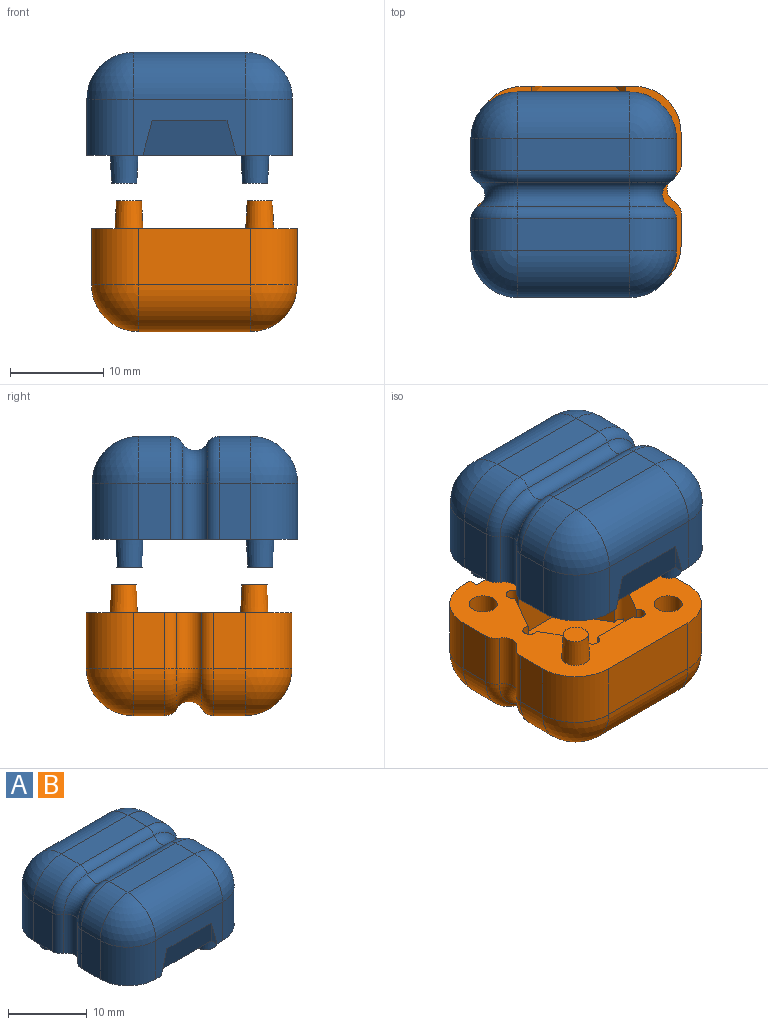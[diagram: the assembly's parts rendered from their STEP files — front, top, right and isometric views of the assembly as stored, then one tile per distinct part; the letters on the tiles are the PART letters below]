
ASSEMBLY  parts=2 mates=1
PART A: 62 faces, bbox 22.8x22x14.4 mm
  f0: plane 12x6mm, normal (0,-1,0), area 38.4mm2, adj f4,f13,f19,f22,f49,f50,f51
  f1: plane 6x3.4mm, normal (1,0,0), area 20.4mm2, adj f4,f16,f20,f52
  f2: plane 6x3.4mm, normal (-1,0,0), area 20.4mm2, adj f4,f5,f13,f61
  f3: plane 12x3.4mm, normal (0,0,1), area 40.8mm2, adj f14,f15,f20,f54
  f4: plane 22x22mm, normal (0,0,-1), area 284.7mm2, adj f0,f1,f2,f7,f8,f9,f11,f13
  f5: cylinder r=5mm len=5mm, axis (0,1,0), area 26.7mm2, adj f2,f10,f17,f60
  f6: cylinder r=5mm len=5mm, axis (0,-1,0), area 26.7mm2, adj f7,f10,f21,f58
  f7: plane 6x3.4mm, normal (1,0,0), area 20.4mm2, adj f4,f6,f22,f57
  f8: plane 12x6mm, normal (0,1,0), area 72mm2, adj f4,f11,f15,f16
  f9: plane 6x3.4mm, normal (-1,0,0), area 20.4mm2, adj f4,f11,f14,f56
  f10: plane 12x3.4mm, normal (0,0,1), area 40.8mm2, adj f5,f6,f19,f59
  f11: cylinder r=5mm len=6mm, axis (0,0,-1), area 47.1mm2, adj f4,f8,f9,f12
  f12: sphere r=5mm, area 39.3mm2, adj f11,f14,f15
  f13: cylinder r=5mm len=6mm, axis (0,0,1), area 47.1mm2, adj f0,f2,f4,f17
  f14: cylinder r=5mm len=5mm, axis (0,1,0), area 26.7mm2, adj f3,f9,f12,f55
  f15: cylinder r=5mm len=12mm, axis (1,0,0), area 94.2mm2, adj f3,f8,f12,f18
  f16: cylinder r=5mm len=6mm, axis (0,0,1), area 47.1mm2, adj f1,f4,f8,f18
  f17: sphere r=5mm, area 39.3mm2, adj f5,f13,f19
  f18: sphere r=5mm, area 39.3mm2, adj f15,f16,f20
  f19: cylinder r=5mm len=12mm, axis (-1,0,0), area 94.2mm2, adj f0,f10,f17,f21
  f20: cylinder r=5mm len=5mm, axis (0,-1,0), area 26.7mm2, adj f1,f3,f18,f53
  f21: sphere r=5mm, area 39.3mm2, adj f6,f19,f22
  f22: cylinder r=5mm len=6mm, axis (0,0,-1), area 47.1mm2, adj f0,f4,f7,f21
  f23: cylinder r=1.5mm len=6mm, axis (0,0,-1), area 18.8mm2, adj f4,f27,f56,f61
  f24: cylinder r=1.5mm len=6mm, axis (0,0,1), area 18.8mm2, adj f4,f25,f52,f57
  f25: torus R=5mm, axis (0,-1,0), area 18.6mm2, adj f24,f26,f53,f58
  f26: cylinder r=1.5mm len=12mm, axis (-1,0,0), area 37.7mm2, adj f25,f27,f54,f59
  f27: torus R=5mm, axis (0,-1,0), area 18.6mm2, adj f23,f26,f55,f60
  f28: cylinder r=0.75mm len=6mm, axis (0,0,-1), area 18.8mm2, adj f4,f29,f39,f40
  f29: plane 6x5.43mm, normal (0,1,0), area 32.6mm2, adj f4,f28,f30,f40
  f30: cylinder r=0.75mm len=6mm, axis (0,0,-1), area 18.8mm2, adj f4,f29,f31,f40
  f31: plane 6x4.7mm, normal (0.87,0.5,0), area 32.6mm2, adj f4,f30,f32,f40
  f32: cylinder r=0.75mm len=6mm, axis (0,0,-1), area 18.8mm2, adj f4,f31,f33,f40
  f33: plane 6x4.7mm, normal (0.87,-0.5,0), area 32.6mm2, adj f4,f32,f34,f40
  f34: cylinder r=0.75mm len=6mm, axis (0,0,-1), area 18.8mm2, adj f4,f33,f35,f40
  f35: plane 6x5.43mm, normal (0,-1,0), area 32.6mm2, adj f4,f34,f36,f40
  f36: cylinder r=0.75mm len=6mm, axis (0,0,-1), area 18.8mm2, adj f4,f35,f37,f40
  f37: plane 6x4.7mm, normal (-0.87,-0.5,0), area 32.6mm2, adj f4,f36,f38,f40
  f38: cylinder r=0.75mm len=6mm, axis (0,0,-1), area 18.8mm2, adj f4,f37,f39,f40
  f39: plane 6x4.7mm, normal (-0.87,0.5,0), area 32.6mm2, adj f4,f28,f38,f40
  f40: plane 15.36x13.5mm, normal (0,0,-1), area 131.8mm2, adj f28,f29,f30,f31,f32,f33,f34,f35
  f41: cone r=1.5mm half-angle=3deg, axis (0,0,1), area 26.8mm2, adj f4,f42
  f42: plane 2.69x2.69mm, normal (0,0,-1), area 5.7mm2, adj f41
  f43: cone r=1.5mm half-angle=3deg, axis (0,0,1), area 26.8mm2, adj f4,f44
  f44: plane 2.69x2.69mm, normal (0,0,-1), area 5.7mm2, adj f43
  f45: cylinder r=1.5mm len=3mm, axis (0,0,-1), area 28.3mm2, adj f4,f46
  f46: plane 3x3mm, normal (0,0,-1), area 7.1mm2, adj f45
  f47: cylinder r=1.5mm len=3mm, axis (0,0,-1), area 28.3mm2, adj f4,f48
  f48: plane 3x3mm, normal (0,0,-1), area 7.1mm2, adj f47
  f49: plane 10x3.73mm, normal (0,-0.97,-0.26), area 34.8mm2, adj f0,f4,f50,f51
  f50: plane 3.73x1mm, normal (0.97,0,-0.26), area 1.9mm2, adj f0,f4,f49
  f51: plane 3.73x1mm, normal (-0.97,0,-0.26), area 1.9mm2, adj f0,f4,f49
  f52: cylinder r=1.5mm len=6mm, axis (0,0,1), area 9.4mm2, adj f1,f4,f24,f53
  f53: torus R=3.5mm, axis (0,1,0), area 11.7mm2, adj f20,f25,f52,f54
  f54: cylinder r=1.5mm len=12mm, axis (-1,0,0), area 18.8mm2, adj f3,f26,f53,f55
  f55: torus R=3.5mm, axis (0,1,0), area 11.7mm2, adj f14,f27,f54,f56
  f56: cylinder r=1.5mm len=6mm, axis (0,0,-1), area 9.4mm2, adj f4,f9,f23,f55
  f57: cylinder r=1.5mm len=6mm, axis (0,0,1), area 9.4mm2, adj f4,f7,f24,f58
  f58: torus R=3.5mm, axis (0,-1,0), area 11.7mm2, adj f6,f25,f57,f59
  f59: cylinder r=1.5mm len=12mm, axis (-1,0,0), area 18.8mm2, adj f10,f26,f58,f60
  f60: torus R=3.5mm, axis (0,-1,0), area 11.7mm2, adj f5,f27,f59,f61
  f61: cylinder r=1.5mm len=6mm, axis (0,0,-1), area 9.4mm2, adj f2,f4,f23,f60
PART B: same geometry as A
PLACE A t=(-0.13,1.55,17.3)mm
PLACE B rot(axis=(1,0,0),180deg) t=(0.38,2.17,9.42)mm
MATE parallel B.f4 <-> A.f4  axis (0,0,1) through (0.38,1.8,9.42)mm
